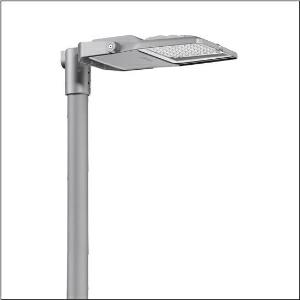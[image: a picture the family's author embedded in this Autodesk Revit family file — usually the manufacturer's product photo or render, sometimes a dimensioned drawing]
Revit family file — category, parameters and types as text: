
# Revit family: floodlight_fl_21_mini___pl64_5xa7776d2e3a_9c1a
name_source: partatom
category: Lighting Fixtures
units: mm (PartAtom-declared; Revit-internal decimal feet)

## family parameters
Cut with Voids When Loaded = No
Host = Face
Light Source = No
Part Type = Normal
Room Calculation Point = No
Round Connector Dimension = Use Diameter
Shared = No

## types (1)
- --- (1 x LED, 17220 lm, 142.9 W, 3000K)
    Apparent Load = 143 VA
    CIE Flux Codes = 28 80 98 100 100
    Color Rendering = 70
    Color Temperature = 3000K
    Default Elevation = 1800 mm
    Description = Floodlight FL 21 mini, floodlight, primary light control with lens, of PMMA, primary optical cover: protective disc, of toughened safety glass, transparent, light distribution: PL64, light emission: direct distribution, installation type: surface-mounted, LED, High Power LED, rated luminous flux: 17.220lm, luminous efficacy: 121lm/W, light colour: 730, colour temperature: 3000K, control gear: Smart Interface (Zhaga), control: flexible luminous flux parameterisation, time-dependent luminous flux control, constant luminous flux control, overheat protection, pre-setting: logarithmic dimming characteristic, with terminal, 6-pole, mains connection: 220..240V, AC, 50/60Hz, start of lifetime: 143W, end of service life: 151W, reduction: 63W, luminaire housing, of diecast aluminium, powder-coated, SITECO metallic grey (DB 702S), corrosivity category C5 mid according to DIN EN ISO 12944, suitable for swimming pools, chlorine-resistant, sealing non-destructively replaceable, please order mast flange separately, mast bracket, of steel, galvanised, powder-coated, SITECO metallic grey (DB 702S), Smart Interface below and above, protection rating (complete): IP66, insulation class (complete): insulation class II (safety insulation), certification: CE, ENEC, VDE, protection symbol: D, impact resistance: IK08, permissible operating ambient temperature: -40..+40°C, permissible operating ambient temperature for outdoor applications: -40..+50°C, standard: DIN EN 12944, LABS conformity tested according to VDMA 24364:2018-05, packaging unit: 1 piece

Light Distribution: PL64
    Height = 70 mm
    Lamp = 1 x LED
    Lamp Light Flux = 17220 lm
    Lamp Power = 142.9 W
    Lamp count = 1
    Length = 485 mm
    Luminous efficacy = 121 lm/W
    Manufacturer = Siteco
    ModVariant = No
    Model = 5XA7776D2E3A
    Mounting Place = Pole
    Mounting Type = Pole annexe
    Number of Poles = 1
    OnlyDefault = Yes
    Power Factor = 1
    Product Name = Floodlight FL 21 mini | PL64
    Product group = floodlight | pylon annexe
    ProductGroupID = 6201
    Protection Class = Protection class II
    Protection Degree = IP 66
    RLX_Detail_Level = 1
    RLX_Emergency_Light_Flux = 0 lm
    RLX_Emergency_Type = 0
    RLX_Emergency_Type_DB = No
    RlxData = <blob elided: 101457 chars, md5=fbe0ac79>
    Socket = socket
    Standby Power = 0 W
    System Light Flux = 17220 lm
    System Power = 143 W
    Type Comments = factory setting: luminous flux: 100 % | dim-lin: 254 | 730 mA
    Type Image = l_1007125.jpg
    URL = http://relux.com
    VarID = @adj_166229
    Voltage = 0 V
    Weight = 0.00 kg
    Width = 337 mm

## geometry (parser evidence)
native form markers: Blend x4, Sweep x12
no freeform markers — native parametric forms only
